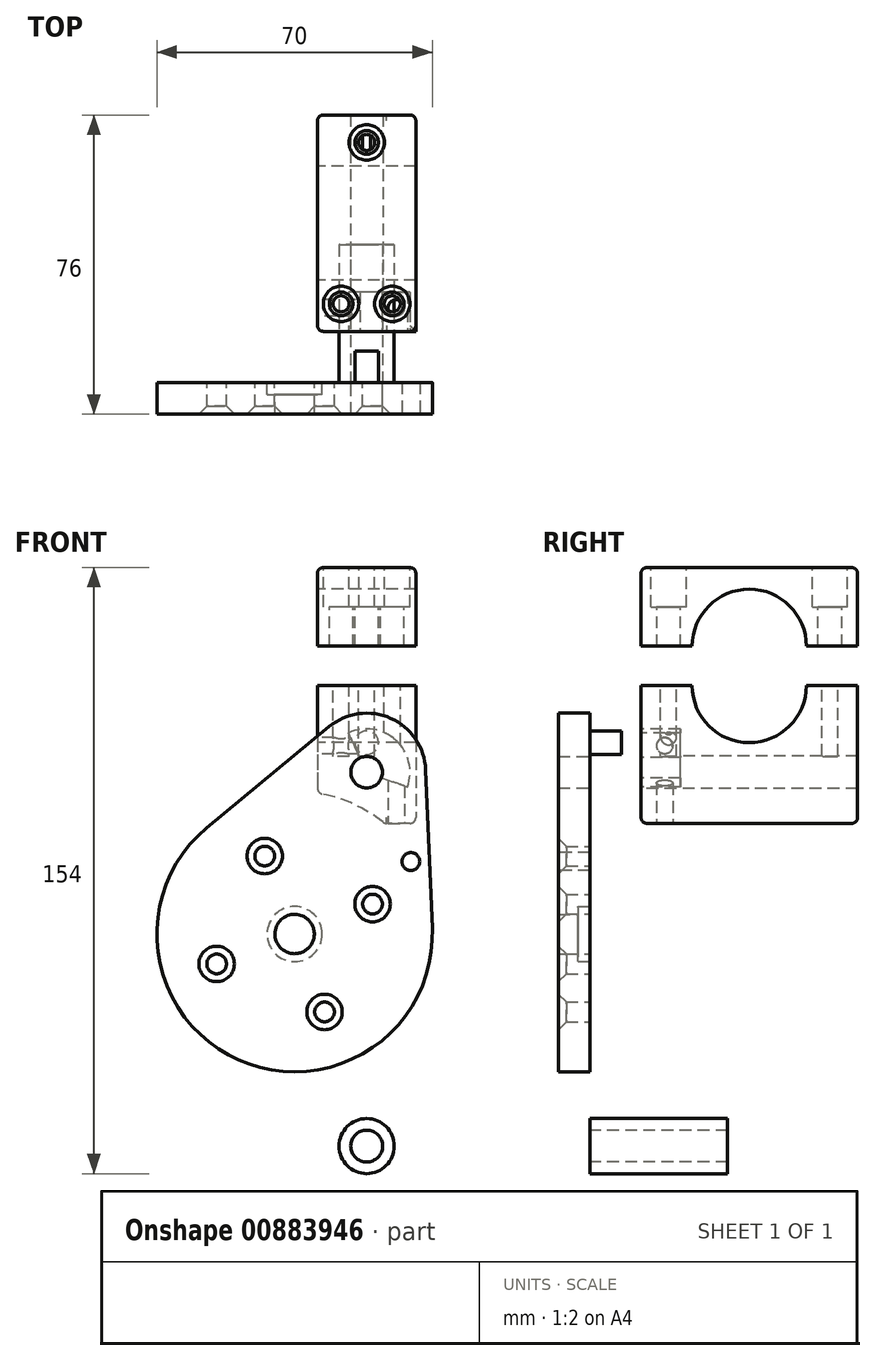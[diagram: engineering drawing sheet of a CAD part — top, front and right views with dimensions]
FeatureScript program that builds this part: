
annotation { "Feature Type Name" : "Feature", "Feature Type Description" : "" }
export const myFeature = defineFeature(function(context is Context, id is Id, definition is map)
    precondition{}
    {
        {
            var Q0;
            Q0=qCreatedBy(makeId("Front.planeOp"),FACE);
            var sketch = newSketch(context, id + "F0", { "sketchPlane" : qUnion([Q0])});
            skCircle(sketch, "E0", {"center": v(0, 0) * mm, "radius": 31.5 * mm, "construction": true});
            skArc(sketch, "E1", {"start": v(-31.35, 15.56) * mm, "mid": v(0, -35) * mm, "end": v(31.35, 15.56) * mm});
            skLineSegment(sketch, "E2.bottom", {"start": v(-15, 15) * mm, "end": v(15, 15) * mm, "construction": true});
            skLineSegment(sketch, "E2.top", {"start": v(-15, -15) * mm, "end": v(15, -15) * mm, "construction": true});
            skLineSegment(sketch, "E2.left", {"start": v(-15, 15) * mm, "end": v(-15, -15) * mm, "construction": true});
            skLineSegment(sketch, "E2.right", {"start": v(15, 15) * mm, "end": v(15, -15) * mm, "construction": true});
            skCircle(sketch, "E3", {"center": v(-15, 15) * mm, "radius": 2.5 * mm});
            skCircle(sketch, "E4", {"center": v(15, 15) * mm, "radius": 2.5 * mm});
            skCircle(sketch, "E5", {"center": v(-15, -15) * mm, "radius": 2.5 * mm});
            skCircle(sketch, "E6", {"center": v(15, -15) * mm, "radius": 2.5 * mm});
            skArc(sketch, "E7", {"start": v(13.44, 51.67) * mm, "mid": v(0, 60) * mm, "end": v(-13.44, 51.67) * mm});
            skLineSegment(sketch, "E8", {"start": v(-31.35, 15.56) * mm, "end": v(-13.44, 51.67) * mm});
            skLineSegment(sketch, "E9", {"start": v(13.44, 51.67) * mm, "end": v(31.35, 15.56) * mm});
            skCircle(sketch, "E10", {"center": v(0, 45) * mm, "radius": 4 * mm});
            skCircle(sketch, "E11", {"center": v(0, 0) * mm, "radius": 5 * mm});
            skSolve(sketch);
        }
        {
            var Q0;
            Q0 = qSketchRegion(id + "F0", true);
            extrude(context, id + "F1", {"entities" : qUnion([Q0]), "depth" : 8 * mm, "offsetDistance" : 25 * mm});
        }
        {
            var Q0;
            Q0=qCreatedBy(makeId("Right.planeOp"),FACE);
            var sketch = newSketch(context, id + "F2", { "sketchPlane" : qUnion([Q0])});
            skLineSegment(sketch, "E12.bottom", {"start": v(0, 97) * mm, "end": v(55, 97) * mm});
            skLineSegment(sketch, "E12.top", {"start": v(0, 32) * mm, "end": v(55, 32) * mm});
            skLineSegment(sketch, "E12.left", {"start": v(0, 97) * mm, "end": v(0, 77) * mm});
            skLineSegment(sketch, "E12.right", {"start": v(55, 97) * mm, "end": v(55, 77) * mm});
            skArc(sketch, "E13", {"start": v(42, 77) * mm, "mid": v(27.5, 91.5) * mm, "end": v(13, 77) * mm});
            skLineSegment(sketch, "E14", {"start": v(0, 77) * mm, "end": v(13, 77) * mm});
            skLineSegment(sketch, "E15", {"start": v(0, 67) * mm, "end": v(13, 67) * mm});
            skLineSegment(sketch, "E16.trimOffspring", {"start": v(0, 67) * mm, "end": v(0, 32) * mm});
            skLineSegment(sketch, "E17.trimOffspring", {"start": v(55, 67) * mm, "end": v(55, 32) * mm});
            skPoint(sketch, "E18", {"position": v(27.5, 67) * mm});
            skLineSegment(sketch, "E19.trimOffspring", {"start": v(42, 77) * mm, "end": v(55, 77) * mm});
            skArc(sketch, "E20", {"start": v(13, 67) * mm, "mid": v(27.5, 52.5) * mm, "end": v(42, 67) * mm});
            skLineSegment(sketch, "E21.trimOffspring", {"start": v(42, 67) * mm, "end": v(55, 67) * mm});
            skSolve(sketch);
        }
        {
            var Q0;
            Q0 = qSketchRegion(id + "F2", true);
            extrude(context, id + "F3", {"entities" : qUnion([Q0]), "endBound" : BoundingType.SYMMETRIC, "depth" : 25 * mm, "offsetDistance" : 25 * mm});
        }
        {
            var Q0;
            Q0=makeQuery(id+"F1.opExtrude","CAP_EDGE",EDGE,{"disambiguationData":[OSD([sQuery(id+"F0.wireOp",EDGE,"E4")])],"isStart":false});
            var Q1;
            Q1=makeQuery(id+"F1.opExtrude","CAP_EDGE",EDGE,{"disambiguationData":[OSD([sQuery(id+"F0.wireOp",EDGE,"E6")])],"isStart":false});
            var Q2;
            Q2=makeQuery(id+"F1.opExtrude","CAP_EDGE",EDGE,{"disambiguationData":[OSD([sQuery(id+"F0.wireOp",EDGE,"E5")])],"isStart":false});
            var Q3;
            Q3=makeQuery(id+"F1.opExtrude","CAP_EDGE",EDGE,{"disambiguationData":[OSD([sQuery(id+"F0.wireOp",EDGE,"E3")])],"isStart":false});
            chamfer(context, id + "F4", {"entities" : qUnion([Q0, Q1, Q2, Q3]), "width" : 2 * mm, "tangentPropagation" : true});
        }
        {
            var Q0;
            Q0=makeQuery(id+"F3.opExtrude","SWEPT_FACE",FACE,{"disambiguationData":[OSD([sQuery(id+"F2.wireOp",EDGE,"E16.trimOffspring")])]});
            var sketch = newSketch(context, id + "F5", { "sketchPlane" : qUnion([Q0])});
            skCircle(sketch, "E22", {"center": v(0, 45) * mm, "radius": 4.12 * mm});
            skSolve(sketch);
        }
        {
            var Q0;
            Q0 = qSketchRegion(id + "F5", true);
            extrude(context, id + "F6", {"entities" : qUnion([Q0]), "operationType" : NewBodyOperationType.REMOVE, "endBound" : BoundingType.THROUGH_ALL, "oppositeDirection" : true, "depth" : 25 * mm, "offsetDistance" : 25 * mm});
        }
        {
            var Q0;
            Q0=makeQuery(id+"F1.opExtrude","CAP_FACE",FACE,{"disambiguationData":[OSD([sQuery(id+"F0.wireOp",EDGE,"E1"),sQuery(id+"F0.wireOp",EDGE,"E3"),sQuery(id+"F0.wireOp",EDGE,"E4"),sQuery(id+"F0.wireOp",EDGE,"E5"),sQuery(id+"F0.wireOp",EDGE,"E6"),sQuery(id+"F0.wireOp",EDGE,"E7"),sQuery(id+"F0.wireOp",EDGE,"E8"),sQuery(id+"F0.wireOp",EDGE,"E9"),sQuery(id+"F0.wireOp",EDGE,"E10"),sQuery(id+"F0.wireOp",EDGE,"E11")])],"isStart":true});
            var sketch = newSketch(context, id + "F7", { "sketchPlane" : qUnion([Q0])});
            skCircle(sketch, "E23", {"center": v(0, 0) * mm, "radius": 7 * mm});
            skSolve(sketch);
        }
        {
            var Q0;
            Q0 = qSketchRegion(id + "F7", true);
            extrude(context, id + "F8", {"entities" : qUnion([Q0]), "operationType" : NewBodyOperationType.REMOVE, "oppositeDirection" : true, "depth" : 3 * mm, "offsetDistance" : 25 * mm});
        }
        {
            var Q0;
            Q0=makeQuery(id+"F3.opExtrude","SWEPT_BODY",BODY,{"disambiguationData":[OSD([sQuery(id+"F2.wireOp",EDGE,"E12.top"),sQuery(id+"F2.wireOp",EDGE,"E15"),sQuery(id+"F2.wireOp",EDGE,"E16.trimOffspring"),sQuery(id+"F2.wireOp",EDGE,"E17.trimOffspring"),sQuery(id+"F2.wireOp",EDGE,"E20"),sQuery(id+"F2.wireOp",EDGE,"E21.trimOffspring")])]});
            var Q1;
            Q1=makeQuery(id+"F3.opExtrude","SWEPT_BODY",BODY,{"disambiguationData":[OSD([sQuery(id+"F2.wireOp",EDGE,"E12.bottom"),sQuery(id+"F2.wireOp",EDGE,"E12.left"),sQuery(id+"F2.wireOp",EDGE,"E12.right"),sQuery(id+"F2.wireOp",EDGE,"E13"),sQuery(id+"F2.wireOp",EDGE,"E14"),sQuery(id+"F2.wireOp",EDGE,"E19.trimOffspring")])]});
            var Q2;
            Q2=makeQuery(id+"F3.opExtrude","CAP_VERTEX",VERTEX,{"disambiguationData":[OSD([sQuery(id+"F2.wireOp",EDGE,"E20"),sQuery(id+"F2.wireOp",EDGE,"E21.trimOffspring")])],"isStart":false});
            var Q3;
            Q3=makeQuery(id+"F3.opExtrude","CAP_VERTEX",VERTEX,{"disambiguationData":[OSD([sQuery(id+"F2.wireOp",EDGE,"E17.trimOffspring"),sQuery(id+"F2.wireOp",EDGE,"E21.trimOffspring")])],"isStart":false});
            transform(context, id + "F9", {"entities" : qUnion([Q0, Q1]), "transformType" : TransformType.TRANSLATION_ENTITY, "oppositeDirectionEntity" : false, "transformLine" : qUnion([Q2, Q3]), "makeCopy" : false});
        }
        {
            var Q0;
            Q0=makeQuery(id+"F1.opExtrude","SWEPT_BODY",BODY,{"disambiguationData":[OSD([sQuery(id+"F0.wireOp",EDGE,"E1"),sQuery(id+"F0.wireOp",EDGE,"E3"),sQuery(id+"F0.wireOp",EDGE,"E4"),sQuery(id+"F0.wireOp",EDGE,"E5"),sQuery(id+"F0.wireOp",EDGE,"E6"),sQuery(id+"F0.wireOp",EDGE,"E7"),sQuery(id+"F0.wireOp",EDGE,"E8"),sQuery(id+"F0.wireOp",EDGE,"E9"),sQuery(id+"F0.wireOp",EDGE,"E10"),sQuery(id+"F0.wireOp",EDGE,"E11")])]});
            var Q1;
            Q1=makeQuery(id+"F1.opExtrude","CAP_EDGE",EDGE,{"disambiguationData":[OSD([sQuery(id+"F0.wireOp",EDGE,"E10")])],"isStart":false});
            transform(context, id + "F10", {"entities" : qUnion([Q0]), "transformType" : TransformType.ROTATION, "transformAxis" : qUnion([Q1]), "angle" : 24 * degree, "oppositeDirection" : true, "makeCopy" : false});
        }
        {
            var Q0;
            Q0=makeQuery(id+"F1.opExtrude","CAP_FACE",FACE,{"disambiguationData":[OSD([sQuery(id+"F0.wireOp",EDGE,"E1"),sQuery(id+"F0.wireOp",EDGE,"E3"),sQuery(id+"F0.wireOp",EDGE,"E4"),sQuery(id+"F0.wireOp",EDGE,"E5"),sQuery(id+"F0.wireOp",EDGE,"E6"),sQuery(id+"F0.wireOp",EDGE,"E7"),sQuery(id+"F0.wireOp",EDGE,"E8"),sQuery(id+"F0.wireOp",EDGE,"E9"),sQuery(id+"F0.wireOp",EDGE,"E10"),sQuery(id+"F0.wireOp",EDGE,"E11")])],"isStart":true});
            var sketch = newSketch(context, id + "F11", { "sketchPlane" : qUnion([Q0])});
            skPoint(sketch, "E24.center.orphan", {"position": v(0, 45) * mm});
            skCircle(sketch, "E25", {"center": v(0, 52.5) * mm, "radius": 3 * mm});
            skSolve(sketch);
        }
        {
            var Q0;
            Q0 = qSketchRegion(id + "F11", true);
            extrude(context, id + "F12", {"entities" : qUnion([Q0]), "operationType" : NewBodyOperationType.ADD, "depth" : 8 * mm, "offsetDistance" : 25 * mm});
        }
        {
            var Q0;
            Q0=makeQuery(id+"F3.opExtrude","SWEPT_FACE",FACE,{"disambiguationData":[OSD([sQuery(id+"F2.wireOp",EDGE,"E16.trimOffspring")])]});
            var sketch = newSketch(context, id + "F13", { "sketchPlane" : qUnion([Q0])});
            skLineSegment(sketch, "E26", {"start": v(0, 52.5) * mm, "end": v(0, 45) * mm, "construction": true});
            skLineSegment(sketch, "E27", {"start": v(0, 45) * mm, "end": v(-7.5, 45) * mm});
            skLineSegment(sketch, "E28", {"start": v(0, 45) * mm, "end": v(-4.65, 54.97) * mm});
            skLineSegment(sketch, "E29", {"start": v(0, 45) * mm, "end": v(10.34, 41.24) * mm});
            skArc(sketch, "E30", {"start": v(10.34, 41.24) * mm, "mid": v(7.43, 53.11) * mm, "end": v(-4.65, 54.97) * mm});
            skSolve(sketch);
        }
        {
            var Q0;
            Q0 = qSketchRegion(id + "F13", true);
            extrude(context, id + "F14", {"entities" : qUnion([Q0]), "operationType" : NewBodyOperationType.REMOVE, "oppositeDirection" : true, "depth" : 10 * mm, "offsetDistance" : 25 * mm});
        }
        {
            var Q0;
            Q0=makeQuery(id+"F3.opExtrude","SWEPT_FACE",FACE,{"disambiguationData":[OSD([sQuery(id+"F2.wireOp",EDGE,"E12.top")])]});
            var sketch = newSketch(context, id + "F15", { "sketchPlane" : qUnion([Q0])});
            skCircle(sketch, "E31", {"center": v(7.5, -19) * mm, "radius": 2.08 * mm});
            skSolve(sketch);
        }
        {
            var Q0;
            Q0 = qSketchRegion(id + "F15", true);
            extrude(context, id + "F16", {"entities" : qUnion([Q0]), "operationType" : NewBodyOperationType.REMOVE, "endBound" : BoundingType.UP_TO_NEXT, "oppositeDirection" : true, "depth" : 25 * mm, "offsetDistance" : 25 * mm});
        }
        {
            var Q0;
            Q0=makeQuery(id+"F3.opExtrude","CAP_FACE",FACE,{"disambiguationData":[OSD([sQuery(id+"F2.wireOp",EDGE,"E12.top"),sQuery(id+"F2.wireOp",EDGE,"E15"),sQuery(id+"F2.wireOp",EDGE,"E16.trimOffspring"),sQuery(id+"F2.wireOp",EDGE,"E17.trimOffspring"),sQuery(id+"F2.wireOp",EDGE,"E20"),sQuery(id+"F2.wireOp",EDGE,"E21.trimOffspring")])],"isStart":true});
            var sketch = newSketch(context, id + "F17", { "sketchPlane" : qUnion([Q0])});
            skCircle(sketch, "E32", {"center": v(-19, 51.74) * mm, "radius": 2.08 * mm});
            skSolve(sketch);
        }
        {
            var Q0;
            Q0 = qSketchRegion(id + "F17", true);
            extrude(context, id + "F18", {"entities" : qUnion([Q0]), "operationType" : NewBodyOperationType.REMOVE, "endBound" : BoundingType.UP_TO_NEXT, "oppositeDirection" : true, "depth" : 25 * mm, "offsetDistance" : 25 * mm});
        }
        {
            var Q0;
            Q0=makeQuery(id+"F3.opExtrude","SWEPT_FACE",FACE,{"disambiguationData":[OSD([sQuery(id+"F2.wireOp",EDGE,"E12.bottom")])]});
            var sketch = newSketch(context, id + "F19", { "sketchPlane" : qUnion([Q0])});
            skLineSegment(sketch, "E33", {"start": v(-12.5, 40.5) * mm, "end": v(38.37, 40.5) * mm, "construction": true});
            skCircle(sketch, "E34", {"center": v(0, 61) * mm, "radius": 3 * mm});
            skCircle(sketch, "E35", {"center": v(-6.5, 20) * mm, "radius": 3 * mm});
            skCircle(sketch, "E36", {"center": v(6.5, 20) * mm, "radius": 3 * mm});
            skSolve(sketch);
        }
        {
            var Q0;
            Q0 = qSketchRegion(id + "F19", true);
            extrude(context, id + "F20", {"entities" : qUnion([Q0]), "operationType" : NewBodyOperationType.REMOVE, "endBound" : BoundingType.UP_TO_NEXT, "oppositeDirection" : true, "depth" : 25 * mm, "offsetDistance" : 25 * mm});
        }
        {
            var Q0;
            Q0=makeQuery(id+"F3.opExtrude","SWEPT_FACE",FACE,{"disambiguationData":[OSD([sQuery(id+"F2.wireOp",EDGE,"E12.bottom")])]});
            var sketch = newSketch(context, id + "F21", { "sketchPlane" : qUnion([Q0])});
            skCircle(sketch, "E37", {"center": v(6.5, 20) * mm, "radius": 4.5 * mm});
            skCircle(sketch, "E38", {"center": v(0, 61) * mm, "radius": 4.5 * mm});
            skCircle(sketch, "E39", {"center": v(-6.5, 20) * mm, "radius": 4.5 * mm});
            skSolve(sketch);
        }
        {
            var Q0;
            Q0 = qSketchRegion(id + "F21", true);
            extrude(context, id + "F22", {"entities" : qUnion([Q0]), "operationType" : NewBodyOperationType.REMOVE, "oppositeDirection" : true, "depth" : 10 * mm, "offsetDistance" : 25 * mm});
        }
        {
            var Q0;
            Q0=makeQuery(id+"F3.opExtrude","SWEPT_FACE",FACE,{"disambiguationData":[OSD([sQuery(id+"F2.wireOp",EDGE,"E15")])]});
            var sketch = newSketch(context, id + "F23", { "sketchPlane" : qUnion([Q0])});
            skCircle(sketch, "E40", {"center": v(0, 61) * mm, "radius": 2.05 * mm});
            skLineSegment(sketch, "E41", {"start": v(0, 68) * mm, "end": v(0, 13) * mm, "construction": true});
            skPoint(sketch, "E41.startSnap0", {"position": v(0, 13) * mm});
            skLineSegment(sketch, "E42", {"start": v(0, 40.5) * mm, "end": v(40.26, 40.5) * mm, "construction": true});
            skLineSegment(sketch, "E43", {"start": v(0, 40.5) * mm, "end": v(-40.96, 40.5) * mm, "construction": true});
            skCircle(sketch, "E44", {"center": v(-6.5, 20) * mm, "radius": 2.05 * mm});
            skCircle(sketch, "E45", {"center": v(6.5, 20) * mm, "radius": 2.05 * mm});
            skSolve(sketch);
        }
        {
            var Q0;
            Q0 = qSketchRegion(id + "F23", true);
            extrude(context, id + "F24", {"entities" : qUnion([Q0]), "operationType" : NewBodyOperationType.REMOVE, "oppositeDirection" : true, "depth" : 18 * mm, "offsetDistance" : 25 * mm});
        }
        {
            var Q0;
            Q0=makeQuery(id+"F3.opExtrude","CAP_EDGE",EDGE,{"disambiguationData":[OSD([sQuery(id+"F2.wireOp",EDGE,"E12.bottom")])],"isStart":true});
            var Q1;
            Q1=makeQuery(id+"F3.opExtrude","CAP_EDGE",EDGE,{"disambiguationData":[OSD([sQuery(id+"F2.wireOp",EDGE,"E12.bottom")])],"isStart":false});
            var Q2;
            Q2=makeQuery(id+"F3.opExtrude","SWEPT_EDGE",EDGE,{"disambiguationData":[OSD([sQuery(id+"F2.wireOp",EDGE,"E12.bottom"),sQuery(id+"F2.wireOp",EDGE,"E12.left")])]});
            var Q3;
            Q3=makeQuery(id+"F3.opExtrude","SWEPT_EDGE",EDGE,{"disambiguationData":[OSD([sQuery(id+"F2.wireOp",EDGE,"E12.bottom"),sQuery(id+"F2.wireOp",EDGE,"E12.right")])]});
            var Q4;
            Q4=makeQuery(id+"F3.opExtrude","SWEPT_EDGE",EDGE,{"disambiguationData":[OSD([sQuery(id+"F2.wireOp",EDGE,"E12.top"),sQuery(id+"F2.wireOp",EDGE,"E16.trimOffspring")])]});
            var Q5;
            Q5=makeQuery(id+"F3.opExtrude","CAP_EDGE",EDGE,{"disambiguationData":[OSD([sQuery(id+"F2.wireOp",EDGE,"E12.top")])],"isStart":false});
            var Q6;
            Q6=makeQuery(id+"F3.opExtrude","SWEPT_EDGE",EDGE,{"disambiguationData":[OSD([sQuery(id+"F2.wireOp",EDGE,"E12.top"),sQuery(id+"F2.wireOp",EDGE,"E17.trimOffspring")])]});
            var Q7;
            Q7=makeQuery(id+"F3.opExtrude","CAP_EDGE",EDGE,{"disambiguationData":[OSD([sQuery(id+"F2.wireOp",EDGE,"E16.trimOffspring")])],"isStart":true});
            var Q8;
            Q8=makeQuery(id+"F3.opExtrude","CAP_EDGE",EDGE,{"disambiguationData":[OSD([sQuery(id+"F2.wireOp",EDGE,"E17.trimOffspring")])],"isStart":false});
            var Q9;
            Q9=makeQuery(id+"F3.opExtrude","CAP_EDGE",EDGE,{"disambiguationData":[OSD([sQuery(id+"F2.wireOp",EDGE,"E17.trimOffspring")])],"isStart":true});
            var Q10;
            Q10=makeQuery(id+"F3.opExtrude","CAP_EDGE",EDGE,{"disambiguationData":[OSD([sQuery(id+"F2.wireOp",EDGE,"E12.right")])],"isStart":false});
            var Q11;
            Q11=makeQuery(id+"F3.opExtrude","CAP_EDGE",EDGE,{"disambiguationData":[OSD([sQuery(id+"F2.wireOp",EDGE,"E12.right")])],"isStart":true});
            var Q12;
            Q12=makeQuery(id+"F3.opExtrude","CAP_EDGE",EDGE,{"disambiguationData":[OSD([sQuery(id+"F2.wireOp",EDGE,"E12.left")])],"isStart":false});
            var Q13;
            Q13=makeQuery(id+"F3.opExtrude","CAP_EDGE",EDGE,{"disambiguationData":[OSD([sQuery(id+"F2.wireOp",EDGE,"E12.left")])],"isStart":true});
            fillet(context, id + "F25", {"entities" : qUnion([Q0, Q1, Q2, Q3, Q4, Q5, Q6, Q7, Q8, Q9, Q10, Q11, Q12, Q13]), "radius" : 1.5 * mm, "tangentPropagation" : true, "allowEdgeOverflow" : false});
        }
        {
            var Q0;
            Q0=makeQuery(id+"F3.opExtrude","SWEPT_FACE",FACE,{"disambiguationData":[OSD([sQuery(id+"F2.wireOp",EDGE,"E16.trimOffspring")])]});
            var sketch = newSketch(context, id + "F26", { "sketchPlane" : qUnion([Q0])});
            skCircle(sketch, "E46", {"center": v(-18.3, 4.15) * mm, "radius": 36 * mm});
            skSolve(sketch);
        }
        {
            var Q0;
            Q0 = qSketchRegion(id + "F26", true);
            extrude(context, id + "F27", {"entities" : qUnion([Q0]), "operationType" : NewBodyOperationType.REMOVE, "endBound" : BoundingType.THROUGH_ALL, "oppositeDirection" : true, "depth" : 25 * mm, "offsetDistance" : 25 * mm});
        }
        {
            var Q0;
            Q0=makeQuery(id+"F27.boolean.opBoolean","INTERSECT",EDGE,{"derivedFrom":[makeQuery(id+"F3.opExtrude","CAP_FACE",FACE,{"disambiguationData":[OSD([sQuery(id+"F2.wireOp",EDGE,"E12.top"),sQuery(id+"F2.wireOp",EDGE,"E15"),sQuery(id+"F2.wireOp",EDGE,"E16.trimOffspring"),sQuery(id+"F2.wireOp",EDGE,"E17.trimOffspring"),sQuery(id+"F2.wireOp",EDGE,"E20"),sQuery(id+"F2.wireOp",EDGE,"E21.trimOffspring")])],"isStart":true}),makeQuery(id+"F27.opExtrude","SWEPT_FACE",FACE,{"disambiguationData":[OSD([sQuery(id+"F26.wireOp",EDGE,"E46")])]})]});
            var Q1;
            Q1=makeQuery(id+"F27.boolean.opBoolean","INTERSECT",EDGE,{"derivedFrom":[makeQuery(id+"F3.opExtrude","SWEPT_FACE",FACE,{"disambiguationData":[OSD([sQuery(id+"F2.wireOp",EDGE,"E12.top")])]}),makeQuery(id+"F27.opExtrude","SWEPT_FACE",FACE,{"disambiguationData":[OSD([sQuery(id+"F26.wireOp",EDGE,"E46")])]})]});
            fillet(context, id + "F28", {"entities" : qUnion([Q0, Q1]), "radius" : 1.5 * mm, "tangentPropagation" : true, "allowEdgeOverflow" : false});
        }
        {
            var Q0;
            Q0=makeQuery(id+"F1.opExtrude","CAP_FACE",FACE,{"disambiguationData":[OSD([sQuery(id+"F0.wireOp",EDGE,"E1"),sQuery(id+"F0.wireOp",EDGE,"E3"),sQuery(id+"F0.wireOp",EDGE,"E4"),sQuery(id+"F0.wireOp",EDGE,"E5"),sQuery(id+"F0.wireOp",EDGE,"E6"),sQuery(id+"F0.wireOp",EDGE,"E7"),sQuery(id+"F0.wireOp",EDGE,"E8"),sQuery(id+"F0.wireOp",EDGE,"E9"),sQuery(id+"F0.wireOp",EDGE,"E10"),sQuery(id+"F0.wireOp",EDGE,"E11")])],"isStart":false});
            var sketch = newSketch(context, id + "F29", { "sketchPlane" : qUnion([Q0])});
            skCircle(sketch, "E47", {"center": v(11.23, 22.3) * mm, "radius": 2.26 * mm});
            skSolve(sketch);
        }
        {
            var Q0;
            Q0 = qSketchRegion(id + "F29", true);
            extrude(context, id + "F30", {"entities" : qUnion([Q0]), "operationType" : NewBodyOperationType.REMOVE, "endBound" : BoundingType.THROUGH_ALL, "oppositeDirection" : true, "depth" : 25 * mm, "offsetDistance" : 25 * mm});
        }
        {
            var Q0;
            Q0=qCreatedBy(makeId("Front.planeOp"),FACE);
            var sketch = newSketch(context, id + "F31", { "sketchPlane" : qUnion([Q0])});
            skCircle(sketch, "E48", {"center": v(0, -50) * mm, "radius": 7 * mm});
            skCircle(sketch, "E49", {"center": v(0, -50) * mm, "radius": 4.05 * mm});
            skSolve(sketch);
        }
        {
            var Q0;
            Q0 = qSketchRegion(id + "F31", true);
            extrude(context, id + "F32", {"entities" : qUnion([Q0]), "depth" : -35 * mm, "offsetDistance" : 25 * mm});
        }
    });
